# Revit family: Storage-Teknion-COHD_Overhead_Hinged_Doors-R2021
name_source: partatom
category: Furniture
units: mm (PartAtom-declared; Revit-internal decimal feet)

## family parameters
Always vertical = Yes
Cut with Voids When Loaded = No
OmniClass Number = 23.40.20.00
OmniClass Title = General Furniture and Specialties
Room Calculation Point = No
Shared = Yes
Work Plane-Based = No

## types (2) — shared parameters
Assembly Code = E2020200
Manufacturer = Teknion
Manufacturer Fax = 416.661.4586
Part Number = COHD
Series = Chronicle
Sustainability Data = https://www.teknion.com
URL = www.teknion.com
Unit Weight URL = http://www.teknion.com
Warranty = http://www.teknion.com
zero-valued in all types: Default Elevation

## per-type parameters (varying)
| type | 2H | Description | Distance | Height | Model |
| 1H | No | Chronicle Overhead, Hinged Doors, 1H Height | 5 " | 14.75 " | COHD1H |
| 2H | Yes | Chronicle Overhead, Hinged Doors, 2H Height | 8 " | 28.5 " | COHD2H |

## geometry (parser evidence)
native form markers: Sweep x2
no freeform markers — native parametric forms only
